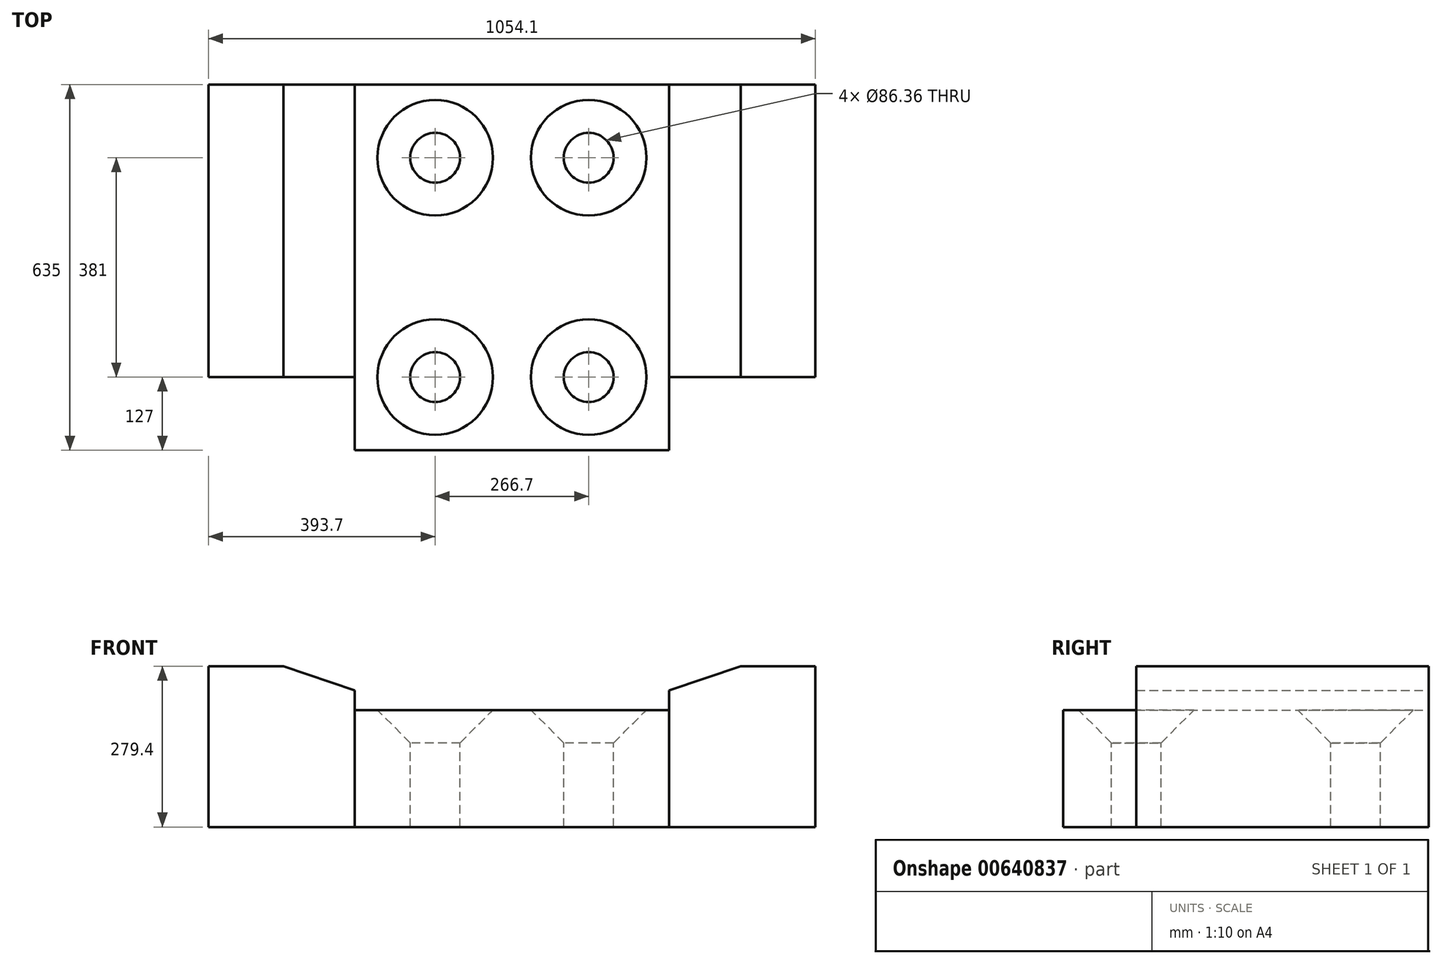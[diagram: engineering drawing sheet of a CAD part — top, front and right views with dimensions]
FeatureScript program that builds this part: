
annotation { "Feature Type Name" : "Feature", "Feature Type Description" : "" }
export const myFeature = defineFeature(function(context is Context, id is Id, definition is map)
    precondition{}
    {
        {
            var Q0;
            Q0=qCreatedBy(makeId("Front.planeOp"),FACE);
            var sketch = newSketch(context, id + "F0", { "sketchPlane" : qUnion([Q0])});
            skLineSegment(sketch, "E0.bottom", {"start": v(0, 0) * mm, "end": v(254, 0) * mm});
            skLineSegment(sketch, "E0.top", {"start": v(0, 279.4) * mm, "end": v(129.8, 279.4) * mm});
            skLineSegment(sketch, "E0.left", {"start": v(0, 0) * mm, "end": v(0, 279.4) * mm});
            skLineSegment(sketch, "E0.right", {"start": v(254, 0) * mm, "end": v(254, 237.35) * mm});
            skLineSegment(sketch, "E1", {"start": v(129.8, 279.4) * mm, "end": v(254, 237.35) * mm});
            skPoint(sketch, "E2.orphan", {"position": v(254, 279.4) * mm});
            skSolve(sketch);
        }
        {
            var Q0;
            Q0 = qSketchRegion(id + "F0", true);
            extrude(context, id + "F1", {"entities" : qUnion([Q0]), "depth" : 508 * mm, "offsetDistance" : 25.4 * mm});
        }
        {
            var Q0;
            Q0=qCreatedBy(makeId("Front.planeOp"),FACE);
            var sketch = newSketch(context, id + "F2", { "sketchPlane" : qUnion([Q0])});
            skLineSegment(sketch, "E3.0.0", {"start": v(129.8, 279.4) * mm, "end": v(0, 279.4) * mm, "construction": true});
            skLineSegment(sketch, "E3.0.1", {"start": v(0, 279.4) * mm, "end": v(0, 0) * mm, "construction": true});
            skLineSegment(sketch, "E3.0.2", {"start": v(0, 0) * mm, "end": v(254, 0) * mm, "construction": true});
            skLineSegment(sketch, "E3.0.3", {"start": v(254, 0) * mm, "end": v(254, 203.2) * mm});
            skLineSegment(sketch, "E3.0.4", {"start": v(254, 237.35) * mm, "end": v(129.8, 279.4) * mm, "construction": true});
            skLineSegment(sketch, "E4.bottom", {"start": v(254, 0) * mm, "end": v(800.1, 0) * mm});
            skLineSegment(sketch, "E4.top", {"start": v(254, 203.2) * mm, "end": v(800.1, 203.2) * mm});
            skLineSegment(sketch, "E4.right", {"start": v(800.1, 0) * mm, "end": v(800.1, 203.2) * mm});
            skSolve(sketch);
        }
        {
            var Q0;
            Q0 = qSketchRegion(id + "F2", true);
            extrude(context, id + "F3", {"entities" : qUnion([Q0]), "operationType" : NewBodyOperationType.ADD, "depth" : 635 * mm, "offsetDistance" : 25.4 * mm});
        }
        {
            var Q0;
            Q0=makeQuery(id+"F3.opExtrude","CAP_FACE",FACE,{"disambiguationData":[OSD([sQuery(id+"F2.wireOp",EDGE,"E3.0.3"),sQuery(id+"F2.wireOp",EDGE,"E4.bottom"),sQuery(id+"F2.wireOp",EDGE,"E4.top"),sQuery(id+"F2.wireOp",EDGE,"E4.right")])],"isStart":false});
            var sketch = newSketch(context, id + "F4", { "sketchPlane" : qUnion([Q0])});
            skLineSegment(sketch, "E5", {"start": v(527.05, 203.2) * mm, "end": v(527.05, 0) * mm});
            skLineSegment(sketch, "E6.0", {"start": v(254, 0) * mm, "end": v(254, 203.2) * mm});
            skLineSegment(sketch, "E7.0", {"start": v(129.8, 279.4) * mm, "end": v(254, 237.35) * mm});
            skLineSegment(sketch, "E8.0", {"start": v(0, 279.4) * mm, "end": v(129.8, 279.4) * mm});
            skPoint(sketch, "E9.0", {"position": v(0, 139.7) * mm});
            skLineSegment(sketch, "E10.0", {"start": v(0, 0) * mm, "end": v(254, 0) * mm});
            skLineSegment(sketch, "E11.0", {"start": v(254, 203.2) * mm, "end": v(254, 237.35) * mm});
            skPoint(sketch, "E12.MirrorP", {"position": v(1054.1, 139.7) * mm});
            skLineSegment(sketch, "E13.MirrorCS", {"start": v(800.1, 0) * mm, "end": v(800.1, 203.2) * mm});
            skLineSegment(sketch, "E14.MirrorCS", {"start": v(924.3, 279.4) * mm, "end": v(800.1, 237.35) * mm});
            skLineSegment(sketch, "E15.MirrorCS", {"start": v(1054.1, 279.4) * mm, "end": v(924.3, 279.4) * mm});
            skLineSegment(sketch, "E16.MirrorCS", {"start": v(1054.1, 0) * mm, "end": v(800.1, 0) * mm});
            skLineSegment(sketch, "E17.MirrorCS", {"start": v(800.1, 203.2) * mm, "end": v(800.1, 237.35) * mm});
            skLineSegment(sketch, "E18", {"start": v(1054.1, 279.4) * mm, "end": v(1054.1, 0) * mm});
            skSolve(sketch);
        }
        {
            var Q0;
            Q0=makeQuery(id+"F3.boolean.opBoolean","MERGE",FACE,{"derivedFrom":[makeQuery(id+"F1.opExtrude","CAP_FACE",FACE,{"disambiguationData":[OSD([sQuery(id+"F0.wireOp",EDGE,"E0.bottom"),sQuery(id+"F0.wireOp",EDGE,"E0.top"),sQuery(id+"F0.wireOp",EDGE,"E0.left"),sQuery(id+"F0.wireOp",EDGE,"E0.right"),sQuery(id+"F0.wireOp",EDGE,"E1")])],"isStart":true}),makeQuery(id+"F3.opExtrude","CAP_FACE",FACE,{"disambiguationData":[OSD([sQuery(id+"F2.wireOp",EDGE,"E3.0.3"),sQuery(id+"F2.wireOp",EDGE,"E4.bottom"),sQuery(id+"F2.wireOp",EDGE,"E4.top"),sQuery(id+"F2.wireOp",EDGE,"E4.right")])],"isStart":true})]});
            var sketch = newSketch(context, id + "F5", { "sketchPlane" : qUnion([Q0])});
            skLineSegment(sketch, "E19.0", {"start": v(-129.8, 279.4) * mm, "end": v(-254, 237.35) * mm});
            skLineSegment(sketch, "E20.0", {"start": v(0, 0) * mm, "end": v(-254, 0) * mm});
            skPoint(sketch, "E21.0", {"position": v(-254, 220.27) * mm});
            skLineSegment(sketch, "E22.0", {"start": v(-254, 203.2) * mm, "end": v(-254, 237.35) * mm});
            skLineSegment(sketch, "E23.0", {"start": v(0, 279.4) * mm, "end": v(-129.8, 279.4) * mm});
            skLineSegment(sketch, "E24.0", {"start": v(0, 0) * mm, "end": v(0, 279.4) * mm});
            skLineSegment(sketch, "E25.0", {"start": v(-254, 0) * mm, "end": v(-254, 203.2) * mm});
            skLineSegment(sketch, "E26.MirrorCS", {"start": v(-1054.1, 0) * mm, "end": v(-1054.1, 279.4) * mm});
            skLineSegment(sketch, "E27.MirrorCS", {"start": v(-800.1, 0) * mm, "end": v(-800.1, 203.2) * mm});
            skLineSegment(sketch, "E28.MirrorCS", {"start": v(-1054.1, 0) * mm, "end": v(-800.1, 0) * mm});
            skLineSegment(sketch, "E29.MirrorCS", {"start": v(-924.3, 279.4) * mm, "end": v(-800.1, 237.35) * mm});
            skLineSegment(sketch, "E30.MirrorCS", {"start": v(-1054.1, 279.4) * mm, "end": v(-924.3, 279.4) * mm});
            skPoint(sketch, "E31.MirrorP", {"position": v(-800.1, 220.27) * mm});
            skLineSegment(sketch, "E32.MirrorCS", {"start": v(-800.1, 203.2) * mm, "end": v(-800.1, 237.35) * mm});
            skSolve(sketch);
        }
        {
            var Q0;
            Q0 = qSketchRegion(id + "F5", true);
            extrude(context, id + "F6", {"entities" : qUnion([Q0]), "operationType" : NewBodyOperationType.ADD, "oppositeDirection" : true, "depth" : 508 * mm, "offsetDistance" : 25.4 * mm});
        }
        {
            var Q0;
            Q0=makeQuery(id+"F3.opExtrude","SWEPT_FACE",FACE,{"disambiguationData":[OSD([sQuery(id+"F2.wireOp",EDGE,"E4.top")])]});
            var sketch = newSketch(context, id + "F7", { "sketchPlane" : qUnion([Q0])});
            skLineSegment(sketch, "E33.bottom", {"start": v(660.4, -508) * mm, "end": v(393.7, -508) * mm});
            skLineSegment(sketch, "E33.top", {"start": v(660.4, -127) * mm, "end": v(393.7, -127) * mm});
            skLineSegment(sketch, "E33.left", {"start": v(660.4, -508) * mm, "end": v(660.4, -127) * mm});
            skLineSegment(sketch, "E33.right", {"start": v(393.7, -508) * mm, "end": v(393.7, -127) * mm});
            skPoint(sketch, "E34", {"position": v(660.4, -508) * mm});
            skPoint(sketch, "E35", {"position": v(393.7, -508) * mm});
            skPoint(sketch, "E36", {"position": v(393.7, -127) * mm});
            skPoint(sketch, "E37", {"position": v(660.4, -127) * mm});
            skSolve(sketch);
        }
        {
            var Q0;
            Q0=sQuery(id+"F7.wireOp",VERTEX,"E34");
            var Q1;
            Q1=sQuery(id+"F7.wireOp",VERTEX,"E35");
            var Q2;
            Q2=sQuery(id+"F7.wireOp",VERTEX,"E36");
            var Q3;
            Q3=sQuery(id+"F7.wireOp",VERTEX,"E37");
            var Q4;
            Q4=makeQuery(id+"F1.opExtrude","SWEPT_BODY",BODY,{"disambiguationData":[OSD([sQuery(id+"F0.wireOp",EDGE,"E0.bottom"),sQuery(id+"F0.wireOp",EDGE,"E0.top"),sQuery(id+"F0.wireOp",EDGE,"E0.left"),sQuery(id+"F0.wireOp",EDGE,"E0.right"),sQuery(id+"F0.wireOp",EDGE,"E1")])]});
            hole(context, id + "F8", {"style" : HoleStyle.C_SINK, "endStyle" : HoleEndStyle.THROUGH, "holeDiameter" : 86.36 * mm, "cSinkDiameter" : 200.66 * mm, "cSinkAngle" : 90 * degree, "majorDiameter" : 6.35 * mm, "isTappedThrough" : true, "tappedDepth" : 12.7 * mm, "tapClearance" : 3, "locations" : qUnion([Q0, Q1, Q2, Q3]), "scope" : qUnion([Q4])});
        }
    });
